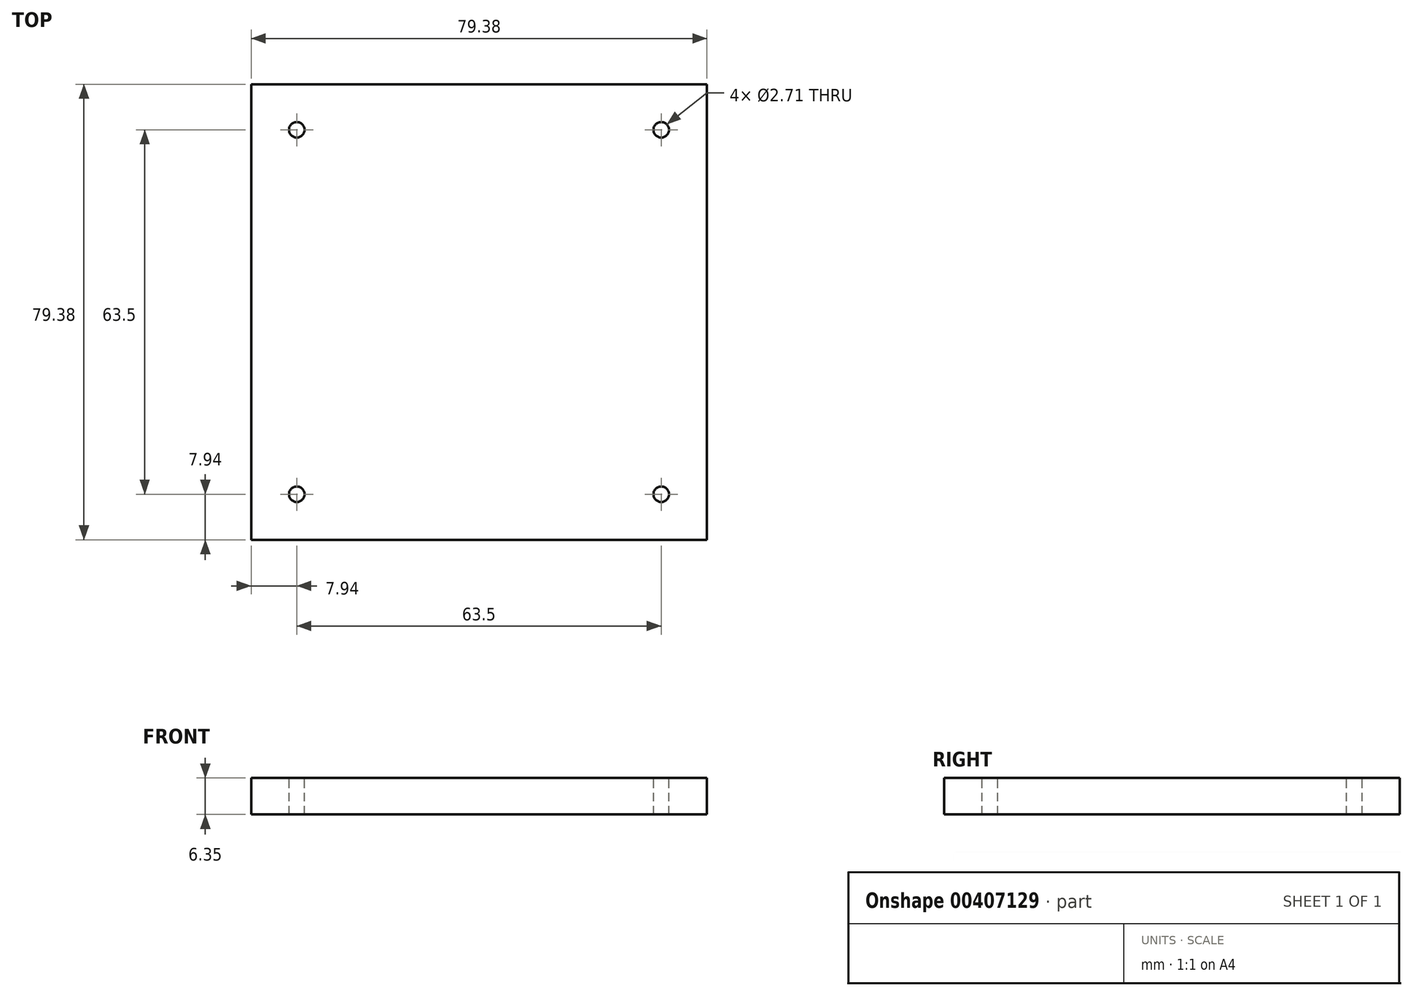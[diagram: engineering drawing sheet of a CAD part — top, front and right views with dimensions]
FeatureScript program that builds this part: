
annotation { "Feature Type Name" : "Feature", "Feature Type Description" : "" }
export const myFeature = defineFeature(function(context is Context, id is Id, definition is map)
    precondition{}
    {
        {
            var Q0;
            Q0=qCreatedBy(makeId("Top.planeOp"),FACE);
            var sketch = newSketch(context, id + "F0", { "sketchPlane" : qUnion([Q0])});
            skLineSegment(sketch, "E0.bottom", {"start": v(39.69, 39.69) * mm, "end": v(-39.69, 39.69) * mm});
            skLineSegment(sketch, "E0.top", {"start": v(39.69, -39.69) * mm, "end": v(-39.69, -39.69) * mm});
            skLineSegment(sketch, "E0.left", {"start": v(39.69, 39.69) * mm, "end": v(39.69, -39.69) * mm});
            skLineSegment(sketch, "E0.right", {"start": v(-39.69, 39.69) * mm, "end": v(-39.69, -39.69) * mm});
            skPoint(sketch, "E0.middle", {"position": v(0, 0) * mm});
            skSolve(sketch);
        }
        {
            var Q0;
            Q0 = qSketchRegion(id + "F0", true);
            extrude(context, id + "F1", {"entities" : qUnion([Q0]), "depth" : 6.35 * mm});
        }
        {
            var Q0;
            Q0=makeQuery(id+"F1.opExtrude","CAP_FACE",FACE,{"disambiguationData":[OSD([sQuery(id+"F0.wireOp",EDGE,"E0.bottom"),sQuery(id+"F0.wireOp",EDGE,"E0.top"),sQuery(id+"F0.wireOp",EDGE,"E0.left"),sQuery(id+"F0.wireOp",EDGE,"E0.right")])],"isStart":false});
            var sketch = newSketch(context, id + "F2", { "sketchPlane" : qUnion([Q0])});
            skLineSegment(sketch, "E1", {"start": v(-39.69, 39.69) * mm, "end": v(39.69, -39.69) * mm, "construction": true});
            skLineSegment(sketch, "E2", {"start": v(39.69, 39.69) * mm, "end": v(-39.69, -39.69) * mm, "construction": true});
            skPoint(sketch, "E3", {"position": v(-31.75, 31.75) * mm});
            skPoint(sketch, "E4", {"position": v(31.75, 31.75) * mm});
            skPoint(sketch, "E5", {"position": v(-31.75, -31.75) * mm});
            skPoint(sketch, "E6", {"position": v(31.75, -31.75) * mm});
            skCircle(sketch, "E7", {"center": v(0, 0) * mm, "radius": 38.1 * mm, "construction": true});
            skSolve(sketch);
        }
        {
            var Q0;
            Q0=sQuery(id+"F2.wireOp",VERTEX,"E3");
            var Q1;
            Q1=sQuery(id+"F2.wireOp",VERTEX,"E5");
            var Q2;
            Q2=sQuery(id+"F2.wireOp",VERTEX,"E6");
            var Q3;
            Q3=sQuery(id+"F2.wireOp",VERTEX,"E4");
            var Q4;
            Q4=makeQuery(id+"F1.opExtrude","SWEPT_BODY",BODY,{"disambiguationData":[OSD([sQuery(id+"F0.wireOp",EDGE,"E0.bottom"),sQuery(id+"F0.wireOp",EDGE,"E0.top"),sQuery(id+"F0.wireOp",EDGE,"E0.left"),sQuery(id+"F0.wireOp",EDGE,"E0.right")])]});
            hole(context, id + "F3", {"style" : HoleStyle.SIMPLE, "endStyle" : HoleEndStyle.THROUGH, "standardTappedOrClearance" : lookupTablePath({ "standard" : "ANSI", "engagement" : "75%", "pitch" : "32 tpi", "size" : "#6", "type" : "Tapped" }), "standardBlindInLast" : lookupTablePath({ "standard" : "ANSI", "engagement" : "75%", "pitch" : "32 tpi", "size" : "#6", "type" : "Tapped" }), "holeDiameter" : 2.7 * mm, "showTappedDepth" : true, "isTappedThrough" : true, "tappedDepth" : 12.7 * mm, "tapClearance" : 3, "startFromSketch" : true, "locations" : qUnion([Q0, Q1, Q2, Q3]), "scope" : qUnion([Q4]), "majorDiameter" : 3.5 * mm});
        }
    });
